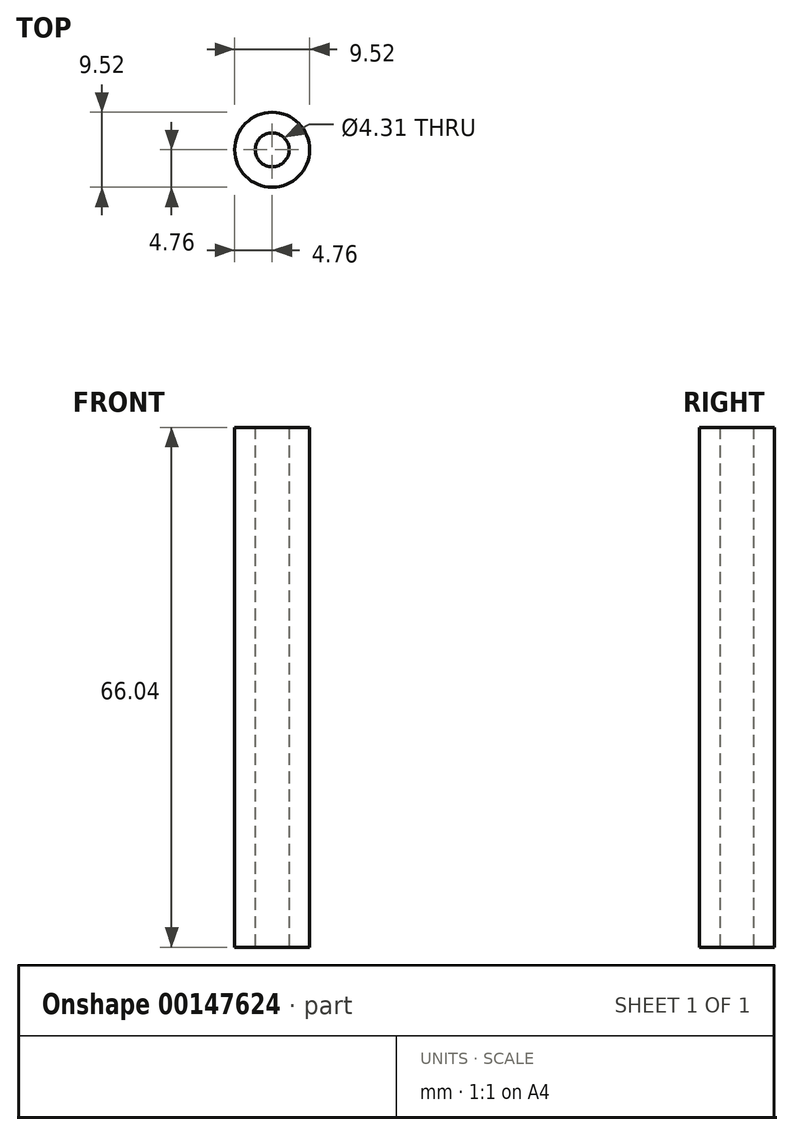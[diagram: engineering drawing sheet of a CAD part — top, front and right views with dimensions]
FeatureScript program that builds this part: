
annotation { "Feature Type Name" : "Feature", "Feature Type Description" : "" }
export const myFeature = defineFeature(function(context is Context, id is Id, definition is map)
    precondition{}
    {
        {
            var Q0;
            Q0=qCreatedBy(makeId("Top.planeOp"),FACE);
            var sketch = newSketch(context, id + "F0", { "sketchPlane" : qUnion([Q0])});
            skCircle(sketch, "E0", {"center": v(0, 0) * mm, "radius": 4.76 * mm});
            skCircle(sketch, "E1", {"center": v(0, 0) * mm, "radius": 2.15 * mm});
            skSolve(sketch);
        }
        {
            var Q0;
            Q0=qSketchRegion(id+"F0",true);
            extrude(context, id + "F1", {"entities" : qUnion([Q0]), "depth" : 66.04 * mm});
        }
    });
